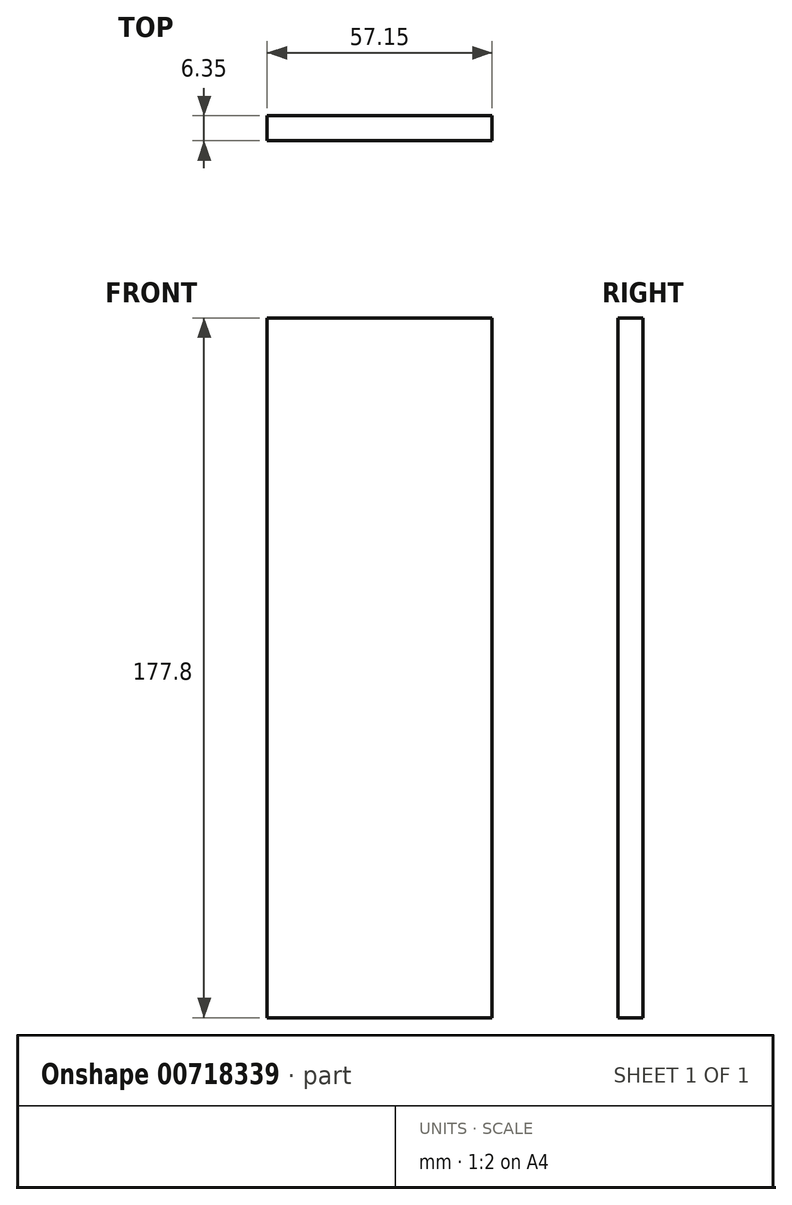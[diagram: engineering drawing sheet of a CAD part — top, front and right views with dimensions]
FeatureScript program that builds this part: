
annotation { "Feature Type Name" : "Feature", "Feature Type Description" : "" }
export const myFeature = defineFeature(function(context is Context, id is Id, definition is map)
    precondition{}
    {
        {
            var Q0;
            Q0=qCreatedBy(makeId("Front.planeOp"),FACE);
            var sketch = newSketch(context, id + "F0", { "sketchPlane" : qUnion([Q0])});
            skLineSegment(sketch, "E0.bottom", {"start": v(0, 0) * mm, "end": v(57.15, 0) * mm});
            skLineSegment(sketch, "E0.top", {"start": v(0, 177.8) * mm, "end": v(57.15, 177.8) * mm});
            skLineSegment(sketch, "E0.left", {"start": v(0, 0) * mm, "end": v(0, 177.8) * mm});
            skLineSegment(sketch, "E0.right", {"start": v(57.15, 0) * mm, "end": v(57.15, 177.8) * mm});
            skSolve(sketch);
        }
        {
            var Q0;
            Q0 = qSketchRegion(id + "F0", true);
            extrude(context, id + "F1", {"entities" : qUnion([Q0]), "depth" : 6.35 * mm, "offsetDistance" : 25.4 * mm});
        }
    });
